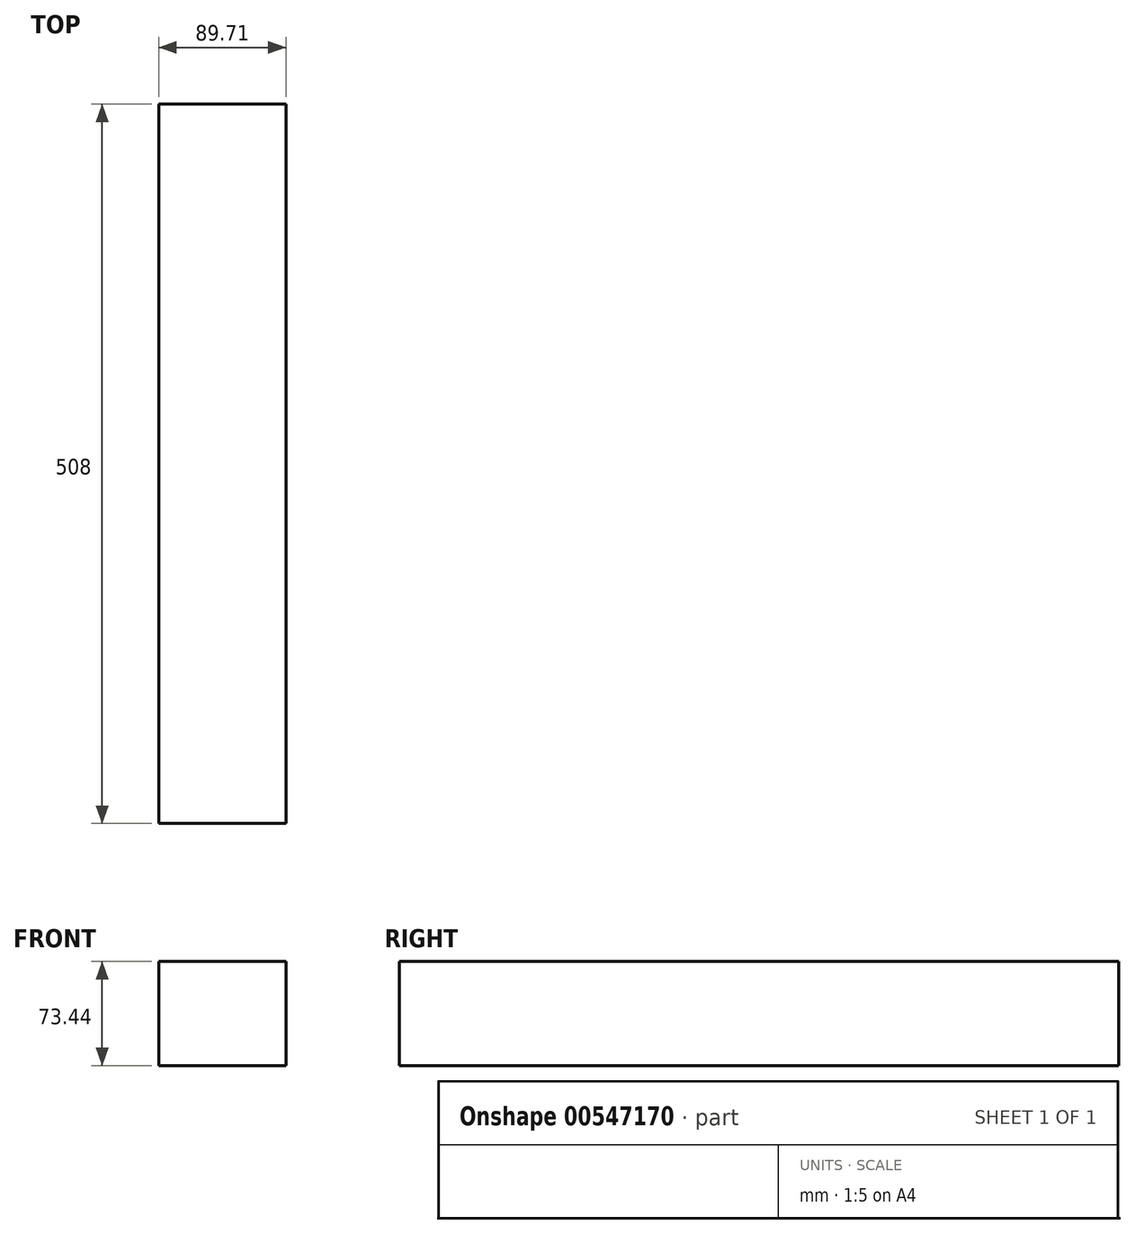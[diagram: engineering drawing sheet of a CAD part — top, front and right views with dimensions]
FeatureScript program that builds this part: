
annotation { "Feature Type Name" : "Feature", "Feature Type Description" : "" }
export const myFeature = defineFeature(function(context is Context, id is Id, definition is map)
    precondition{}
    {
        {
            var Q0;
            Q0=qCreatedBy(makeId("Front.planeOp"),FACE);
            var sketch = newSketch(context, id + "F0", { "sketchPlane" : qUnion([Q0])});
            skLineSegment(sketch, "E0.bottom", {"start": v(0, 0) * mm, "end": v(89.7, 0) * mm});
            skLineSegment(sketch, "E0.top", {"start": v(0, -73.44) * mm, "end": v(89.7, -73.44) * mm});
            skLineSegment(sketch, "E0.left", {"start": v(0, 0) * mm, "end": v(0, -73.44) * mm});
            skLineSegment(sketch, "E0.right", {"start": v(89.7, 0) * mm, "end": v(89.7, -73.44) * mm});
            skSolve(sketch);
        }
        {
            var Q0;
            Q0=makeQuery(id+"F0.imprint","IMPRINT",FACE,{"disambiguationData":[TD([[makeQuery(id+"F0.imprint","IMPRINT",EDGE,{"derivedFrom":sQuery(id+"F0.wireOp",EDGE,"E0.bottom")}),-1.0]])]});
            var Q1;
            Q1=sQuery(id+"F0.wireOp",EDGE,"E0.top");
            var Q2;
            Q2=sQuery(id+"F0.wireOp",EDGE,"E0.bottom");
            var Q3;
            Q3=sQuery(id+"F0.wireOp",EDGE,"E0.right");
            var Q4;
            Q4=sQuery(id+"F0.wireOp",EDGE,"E0.left");
            extrude(context, id + "F1", {"entities" : qUnion([Q0]), "bodyType" : ToolBodyType.SURFACE, "surfaceEntities" : qUnion([Q1, Q2, Q3, Q4]), "oppositeDirection" : true, "depth" : 508 * mm, "offsetDistance" : 25.4 * mm});
        }
    });
